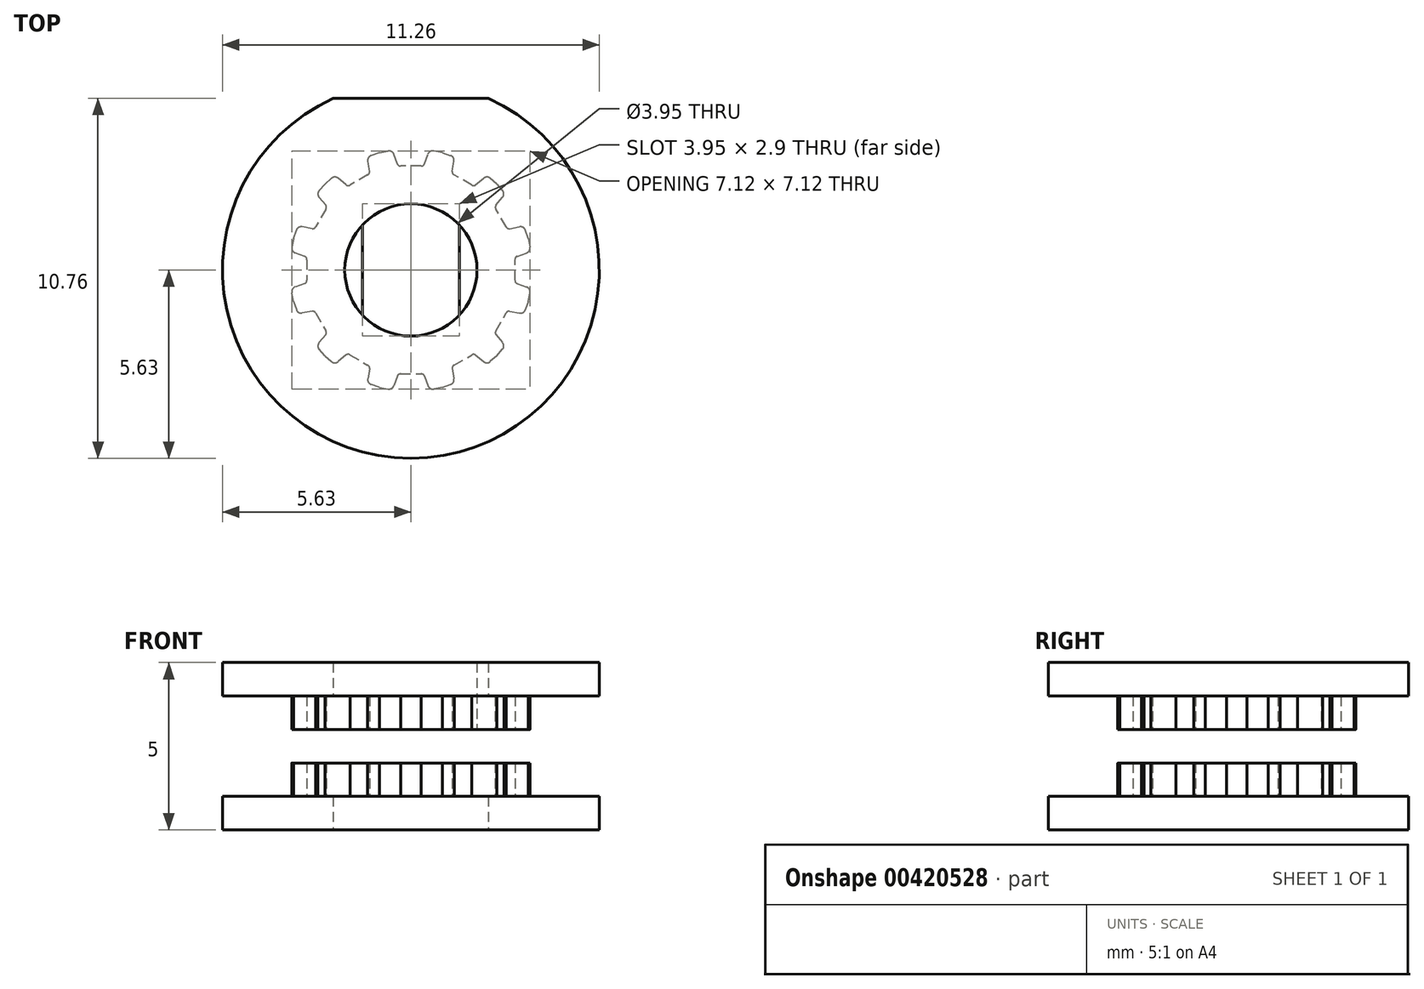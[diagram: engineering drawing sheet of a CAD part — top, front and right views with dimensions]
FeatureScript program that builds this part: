
annotation { "Feature Type Name" : "Feature", "Feature Type Description" : "" }
export const myFeature = defineFeature(function(context is Context, id is Id, definition is map)
    precondition{}
    {
        {
            assignVariable(context, id + "F0", {"name" : "teeth", "anyValue" : 12});
        }
        {
            var Q0;
            Q0=qCreatedBy(makeId("Top.planeOp"),FACE);
            var sketch = newSketch(context, id + "F1", { "sketchPlane" : qUnion([Q0])});
            skCircle(sketch, "E0", {"center": v(0, 0) * mm, "radius": 3.63 * mm, "construction": true});
            skLineSegment(sketch, "E1", {"start": v(0, 0) * mm, "end": v(0, 3.63) * mm, "construction": true});
            skLineSegment(sketch, "E2", {"start": v(0, 0) * mm, "end": v(0.94, 3.5) * mm, "construction": true});
            skArc(sketch, "E3", {"start": v(0.8, 3.02) * mm, "mid": v(0.4, 3.1) * mm, "end": v(0, 3.13) * mm, "construction": true});
            skArc(sketch, "E4", {"start": v(0.94, 3.5) * mm, "mid": v(0, 3.63) * mm, "end": v(-0.94, 3.5) * mm});
            skLineSegment(sketch, "E5", {"start": v(-0.94, 3.5) * mm, "end": v(-1.97, 7.37) * mm});
            skArc(sketch, "E6", {"start": v(1.97, 7.37) * mm, "mid": v(0, 7.63) * mm, "end": v(-1.97, 7.37) * mm});
            skLineSegment(sketch, "E7", {"start": v(1.97, 7.37) * mm, "end": v(0.94, 3.5) * mm});
            skPoint(sketch, "E8", {"position": v(0.38, 3.1) * mm});
            skLineSegment(sketch, "E9", {"start": v(0.4, 3.17) * mm, "end": v(0.51, 3.46) * mm});
            skLineSegment(sketch, "E10", {"start": v(0.94, 3.5) * mm, "end": v(0.68, 3.56) * mm});
            skPoint(sketch, "E11.visualSharp", {"position": v(0.55, 3.58) * mm});
            skArc(sketch, "E11.filletArc", {"start": v(0.68, 3.56) * mm, "mid": v(0.58, 3.54) * mm, "end": v(0.51, 3.46) * mm});
            skArc(sketch, "E12.filletArc", {"start": v(0.3, 3.1) * mm, "mid": v(0.37, 3.12) * mm, "end": v(0.4, 3.17) * mm});
            skLineSegment(sketch, "E13.MirrorCS", {"start": v(-0.4, 3.17) * mm, "end": v(-0.51, 3.46) * mm});
            skArc(sketch, "E14.MirrorCS", {"start": v(-0.3, 3.1) * mm, "mid": v(-0.37, 3.12) * mm, "end": v(-0.4, 3.17) * mm});
            skLineSegment(sketch, "E15.MirrorCS", {"start": v(0, 3.13) * mm, "end": v(-0.3, 3.1) * mm, "construction": true});
            skArc(sketch, "E16.MirrorCS", {"start": v(-0.68, 3.56) * mm, "mid": v(-0.58, 3.54) * mm, "end": v(-0.51, 3.46) * mm});
            skLineSegment(sketch, "E17.MirrorCS", {"start": v(-0.94, 3.5) * mm, "end": v(-0.68, 3.56) * mm});
            skLineSegment(sketch, "E18", {"start": v(0.3, 3.1) * mm, "end": v(-0.3, 3.1) * mm});
            skSolve(sketch);
        }
        {
            var Q0;
            Q0=qCreatedBy(makeId("Top.planeOp"),FACE);
            var sketch = newSketch(context, id + "F2", { "sketchPlane" : qUnion([Q0])});
            skCircle(sketch, "E19", {"center": v(0, 0) * mm, "radius": 5.63 * mm});
            skCircle(sketch, "E20", {"center": v(0, 0) * mm, "radius": 1.98 * mm});
            skLineSegment(sketch, "E21", {"start": v(-1.45, 1.34) * mm, "end": v(-1.45, -1.34) * mm});
            skLineSegment(sketch, "E22", {"start": v(1.45, 1.34) * mm, "end": v(1.45, -1.34) * mm});
            skCircle(sketch, "E23", {"center": v(-3.98, 0) * mm, "radius": 0.5 * mm, "construction": true});
            skCircle(sketch, "E24", {"center": v(3.98, 0) * mm, "radius": 0.5 * mm, "construction": true});
            skLineSegment(sketch, "E25", {"start": v(-3.98, 0) * mm, "end": v(3.98, 0) * mm, "construction": true});
            skLineSegment(sketch, "E26", {"start": v(-2.32, 5.13) * mm, "end": v(2.32, 5.13) * mm});
            skSolve(sketch);
        }
        {
            var Q0;
            Q0=makeQuery(id+"F2.imprint","IMPRINT",FACE,{"disambiguationData":[TD([[makeQuery(id+"F2.imprint","IMPRINT",EDGE,{"derivedFrom":sQuery(id+"F2.wireOp",EDGE,"E23")}),-1.0]])]});
            var Q1;
            {var subQ7=sQuery(id+"F2.wireOp",EDGE,"E26");Q1=makeQuery(id+"F2.imprint","IMPRINT",FACE,{"disambiguationData":[TD([[makeQuery(id+"F2.imprint","IMPRINT",EDGE,{"derivedFrom":subQ7}),-1.0]])]});}
            extrude(context, id + "F3", {"entities" : qUnion([Q0, Q1]), "depth" : 2.5 * mm, "offsetDistance" : 25 * mm});
        }
        {
            var Q0;
            {var subQ7=sQuery(id+"F2.wireOp",EDGE,"E26");Q0=makeQuery(id+"F2.imprint","IMPRINT",FACE,{"disambiguationData":[TD([[makeQuery(id+"F2.imprint","IMPRINT",EDGE,{"derivedFrom":subQ7}),-1.0]])]});}
            var Q1;
            {var subQ0=sQuery(id+"F2.wireOp",EDGE,"E21");Q1=makeQuery(id+"F2.imprint","IMPRINT",FACE,{"disambiguationData":[TD([[makeQuery(id+"F2.imprint","IMPRINT",EDGE,{"derivedFrom":subQ0}),-1.0]])]});}
            var Q2;
            {var subQ0=sQuery(id+"F2.wireOp",EDGE,"E22");Q2=makeQuery(id+"F2.imprint","IMPRINT",FACE,{"disambiguationData":[TD([[makeQuery(id+"F2.imprint","IMPRINT",EDGE,{"derivedFrom":subQ0}),1.0]])]});}
            extrude(context, id + "F4", {"entities" : qUnion([Q0, Q1, Q2]), "operationType" : NewBodyOperationType.ADD, "oppositeDirection" : true, "depth" : 2.5 * mm, "offsetDistance" : 25 * mm});
        }
        {
            var Q0;
            Q0=qSketchRegion(id+"F1",true);
            extrude(context, id + "F5", {"entities" : qUnion([Q0]), "endBound" : BoundingType.SYMMETRIC, "depth" : 3 * mm, "offsetDistance" : 25 * mm});
        }
        {
            var Q0;
            Q0=makeQuery(id+"F5.opExtrude","SWEPT_BODY",BODY,{"disambiguationData":[OSD([sQuery(id+"F1.wireOp",EDGE,"E5"),sQuery(id+"F1.wireOp",EDGE,"E6"),sQuery(id+"F1.wireOp",EDGE,"E7"),sQuery(id+"F1.wireOp",EDGE,"KHEIsP2H-6thQ-GgGZ-kpll-Wur77x7NuSWl"),sQuery(id+"F1.wireOp",EDGE,"E9"),sQuery(id+"F1.wireOp",EDGE,"E10"),sQuery(id+"F1.wireOp",EDGE,"E11.filletArc"),sQuery(id+"F1.wireOp",EDGE,"E12.filletArc"),sQuery(id+"F1.wireOp",EDGE,"E13.MirrorCS"),sQuery(id+"F1.wireOp",EDGE,"E14.MirrorCS"),sQuery(id+"F1.wireOp",EDGE,"E15.MirrorCS"),sQuery(id+"F1.wireOp",EDGE,"E16.MirrorCS"),sQuery(id+"F1.wireOp",EDGE,"E17.MirrorCS")])]});
            var Q1;
            Q1=sQuery(id+"F1.wireOp",EDGE,"E0");
            circularPattern(context, id + "F6", {"operationType" : NewBodyOperationType.REMOVE, "entities" : qUnion([Q0]), "axis" : qUnion([Q1]), "angle" : 360 * degree, "instanceCount" : getVariable(context, 'teeth'), "equalSpace" : true});
        }
        {
            var Q0;
            Q0=qSketchRegion(id+"F2",true);
            var Q1;
            {var subQ0=sQuery(id+"F2.wireOp",EDGE,"E22");Q1=makeQuery(id+"F2.imprint","IMPRINT",FACE,{"disambiguationData":[TD([[makeQuery(id+"F2.imprint","IMPRINT",EDGE,{"derivedFrom":subQ0}),1.0]])]});}
            var Q2;
            {var subQ0=sQuery(id+"F2.wireOp",EDGE,"E21");Q2=makeQuery(id+"F2.imprint","IMPRINT",FACE,{"disambiguationData":[TD([[makeQuery(id+"F2.imprint","IMPRINT",EDGE,{"derivedFrom":subQ0}),1.0]])]});}
            var Q3;
            {var subQ0=sQuery(id+"F2.wireOp",EDGE,"E21");Q3=makeQuery(id+"F2.imprint","IMPRINT",FACE,{"disambiguationData":[TD([[makeQuery(id+"F2.imprint","IMPRINT",EDGE,{"derivedFrom":subQ0}),-1.0]])]});}
            extrude(context, id + "F7", {"entities" : qUnion([Q0, Q1, Q2, Q3]), "operationType" : NewBodyOperationType.REMOVE, "endBound" : BoundingType.SYMMETRIC, "oppositeDirection" : true, "depth" : 1 * mm, "offsetDistance" : 25 * mm});
        }
        {
            var Q0;
            Q0=makeQuery(id+"F7.boolean.opBoolean","SPLIT",BODY,{"disambiguationData":[OD(0.0)],"derivedFrom":makeQuery(id+"F3.opExtrude","SWEPT_BODY",BODY,{"disambiguationData":[OSD([sQuery(id+"F2.wireOp",EDGE,"E19"),sQuery(id+"F2.wireOp",EDGE,"E20"),sQuery(id+"F2.wireOp",EDGE,"E21"),sQuery(id+"F2.wireOp",EDGE,"E22")])]})});
            transform(context, id + "F8", {"entities" : qUnion([Q0]), "transformType" : TransformType.TRANSLATION_3D, "dx" : 0 * mm, "dy" : 0 * mm, "dz" : -10 * mm, "makeCopy" : false});
        }
    });
